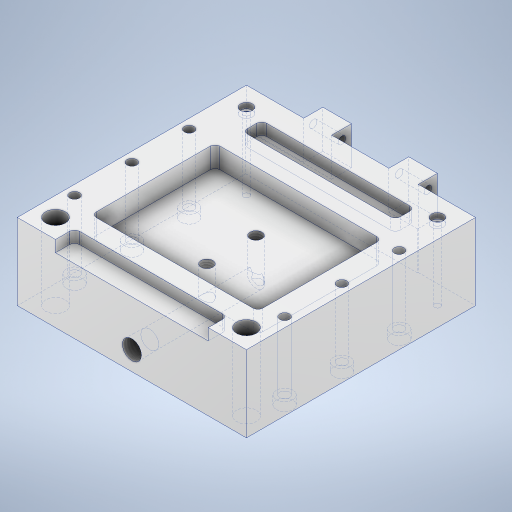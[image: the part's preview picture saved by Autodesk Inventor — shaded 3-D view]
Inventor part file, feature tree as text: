
AUTODESK INVENTOR PART (.ipt)
format: ipt  version: 2023 (Build 270158000, 158)  size: 441,344 bytes
history: native  units: in
note: dims shown in document units (in); Inventor stores cm internally (conversion verified against a paired STEP export)
features: sketch x10, hole x6, extrude x5
ambient origin geometry x8: Origin, YZ Plane, XZ Plane, XY Plane, X Axis, Y Axis, Z Axis, Center Point
bodies: Solid1 (feature_tree)
feature tree (21):
  extrude  "Extrusion1"  Depth=3.25in
  extrude  "Extrusion2"  Depth=0.375in
  extrude  "Extrusion3"  Depth=0.25in
  hole  "Hole1"  [1 undecoded]
  extrude  "Extrusion5"  Depth=0.125in
  hole  "Hole3"  [1 undecoded]
  extrude  "Extrusion6"  Depth=0.5in
  hole  "Hole4"  [1 undecoded]
  hole  "Hole5"  [1 undecoded]
  hole  "Hole6"  [1 undecoded]
  hole  "Hole7"  [1 undecoded]
  sketch  "Sketch1"  dims[d0=3.0in d1=3.25in]
  sketch  "Sketch2"  dims[d2=1.0in d3=0.0in d6=0.375in]
  sketch  "Sketch3"  dims[d7=0.375in d8=0.25in]
  sketch  "Sketch4"  dims[d9=0.75in d10=0.0in d11=0.0in]
  sketch  "Sketch6"  dims[d12=0.0in d13=0.0in d14=0.125in]
  sketch  "Sketch9"  dims[d15=0.125in]
  sketch  "Sketch11"  dims[d16=0.1in d17=0.38in d18=0.375in d19=0.25in d20=0.5635in d21=1.0in d22=0.8108in d25=2.0in]
  sketch  "Sketch12"  dims[d26=0.25in d28=0.5in]
  sketch  "Sketch13"  dims[d29=2.0in d30=0.25in]
  sketch  "Sketch14"  dims[d31=0.5in d32=0.15in d33=0.0in d46=0.0625in d48=0.25in d50=0.25in d51=0.081in d52=0.38in d53=0.156in d54=0.073in d55=0.5635in d56=1.0in d57=0.8108in d58=0.26in d60=0.3in d61=0.25in d62=0.3644in d63=0.5144in d64=2.1813in d65=1.6213in d66=0.2677in d67=0.0in d68=0.0625in d69=0.25in d70=0.25in d71=0.25in d72=0.26in d73=0.146in d74=0.375in d75=0.25in d76=0.5635in d77=1.0in d78=0.8108in d79=0.125in d80=1.375in d81=0.75in d82=0.75in d83=0.129in d84=0.224in d85=0.219in d86=0.112in d87=0.5635in d88=1.0in d89=0.8108in d90=0.156in d91=0.38in d92=0.375in d93=0.1496in d94=0.5635in d95=0.536in d96=0.8108in d97=0.25in d98=0.234in d99=0.2341in d100=0.375in d101=0.25in d102=0.5635in d103=1.625in d104=0.8108in d105=0.0246in d106=0.236in]
note: 6 required parameter values undecoded (feature->parameter linkage not recoverable at this tier; creation-order binding heuristic only, values carry confidence <= 0.55)
